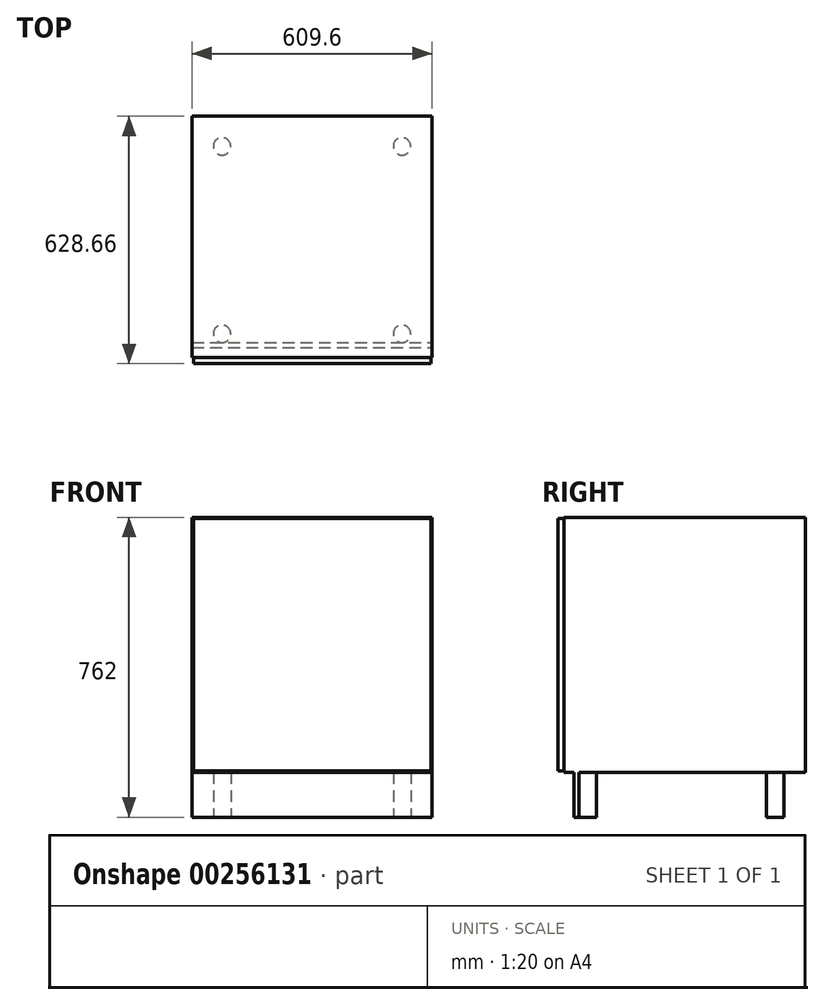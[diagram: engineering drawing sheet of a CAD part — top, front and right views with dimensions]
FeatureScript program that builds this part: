
annotation { "Feature Type Name" : "Feature", "Feature Type Description" : "" }
export const myFeature = defineFeature(function(context is Context, id is Id, definition is map)
    precondition{}
    {
        {
            var Q0;
            Q0=qCreatedBy(makeId("Front.planeOp"),FACE);
            var sketch = newSketch(context, id + "F0", { "sketchPlane" : qUnion([Q0])});
            skLineSegment(sketch, "E0.bottom", {"start": v(304.8, 114.3) * mm, "end": v(-304.8, 114.3) * mm});
            skLineSegment(sketch, "E0.top", {"start": v(304.8, 762) * mm, "end": v(-304.8, 762) * mm});
            skLineSegment(sketch, "E0.left", {"start": v(304.8, 114.3) * mm, "end": v(304.8, 762) * mm});
            skLineSegment(sketch, "E0.right", {"start": v(-304.8, 114.3) * mm, "end": v(-304.8, 762) * mm});
            skPoint(sketch, "E0.middle", {"position": v(0, 438.15) * mm});
            skSolve(sketch);
        }
        {
            var Q0;
            Q0=qSketchRegion(id+"F0",true);
            extrude(context, id + "F1", {"entities" : qUnion([Q0]), "endBound" : BoundingType.SYMMETRIC, "oppositeDirection" : true, "depth" : 628.65 * mm});
        }
        {
            var Q0;
            Q0=qCreatedBy(makeId("Top.planeOp"),FACE);
            var sketch = newSketch(context, id + "F2", { "sketchPlane" : qUnion([Q0])});
            skCircle(sketch, "E1", {"center": v(-228.6, -238.13) * mm, "radius": 22.23 * mm});
            skCircle(sketch, "E2.MirrorC", {"center": v(228.6, -238.13) * mm, "radius": 22.23 * mm});
            skCircle(sketch, "E3.MirrorC", {"center": v(228.6, 238.13) * mm, "radius": 22.23 * mm});
            skCircle(sketch, "E4.MirrorC", {"center": v(-228.6, 238.13) * mm, "radius": 22.23 * mm});
            skSolve(sketch);
        }
        {
            var Q0;
            Q0=qSketchRegion(id+"F2",true);
            extrude(context, id + "F3", {"entities" : qUnion([Q0]), "operationType" : NewBodyOperationType.ADD, "depth" : 114.3 * mm});
        }
        {
            var Q0;
            Q0=qCreatedBy(makeId("Top.planeOp"),FACE);
            var sketch = newSketch(context, id + "F4", { "sketchPlane" : qUnion([Q0])});
            skLineSegment(sketch, "E5.bottom", {"start": v(-304.8, -260.6) * mm, "end": v(304.8, -260.6) * mm});
            skLineSegment(sketch, "E5.top", {"start": v(-304.8, -273.3) * mm, "end": v(304.8, -273.3) * mm});
            skLineSegment(sketch, "E5.left", {"start": v(-304.8, -260.6) * mm, "end": v(-304.8, -273.3) * mm});
            skLineSegment(sketch, "E5.right", {"start": v(304.8, -260.6) * mm, "end": v(304.8, -273.3) * mm});
            skPoint(sketch, "E5.middle", {"position": v(0, -266.95) * mm});
            skSolve(sketch);
        }
        {
            var Q0;
            Q0=qSketchRegion(id+"F4",true);
            extrude(context, id + "F5", {"entities" : qUnion([Q0]), "operationType" : NewBodyOperationType.ADD, "endBound" : BoundingType.UP_TO_NEXT, "depth" : 25.4 * mm});
        }
        {
            var Q0;
            Q0=makeQuery(id+"F1.opExtrude","CAP_FACE",FACE,{"disambiguationData":[OSD([sQuery(id+"F0.wireOp",EDGE,"E0.bottom"),sQuery(id+"F0.wireOp",EDGE,"E0.top"),sQuery(id+"F0.wireOp",EDGE,"E0.left"),sQuery(id+"F0.wireOp",EDGE,"E0.right")])],"isStart":true});
            var sketch = newSketch(context, id + "F6", { "sketchPlane" : qUnion([Q0])});
            skLineSegment(sketch, "E6.0", {"start": v(301.63, 117.48) * mm, "end": v(301.62, 758.83) * mm});
            skLineSegment(sketch, "E6.1", {"start": v(-301.62, 117.47) * mm, "end": v(301.63, 117.48) * mm});
            skLineSegment(sketch, "E6.2", {"start": v(-301.63, 758.83) * mm, "end": v(-301.62, 117.47) * mm});
            skLineSegment(sketch, "E6.3", {"start": v(301.62, 758.83) * mm, "end": v(-301.63, 758.83) * mm});
            skSolve(sketch);
        }
        {
            var Q0;
            Q0=makeQuery(id+"F6.imprint","IMPRINT",FACE,{"disambiguationData":[TD([[makeQuery(id+"F6.imprint","IMPRINT",EDGE,{"derivedFrom":sQuery(id+"F6.wireOp",EDGE,"E6.0")}),-1.0]])]});
            extrude(context, id + "F7", {"entities" : qUnion([Q0]), "operationType" : NewBodyOperationType.REMOVE, "oppositeDirection" : true, "depth" : 15.88 * mm});
        }
    });
